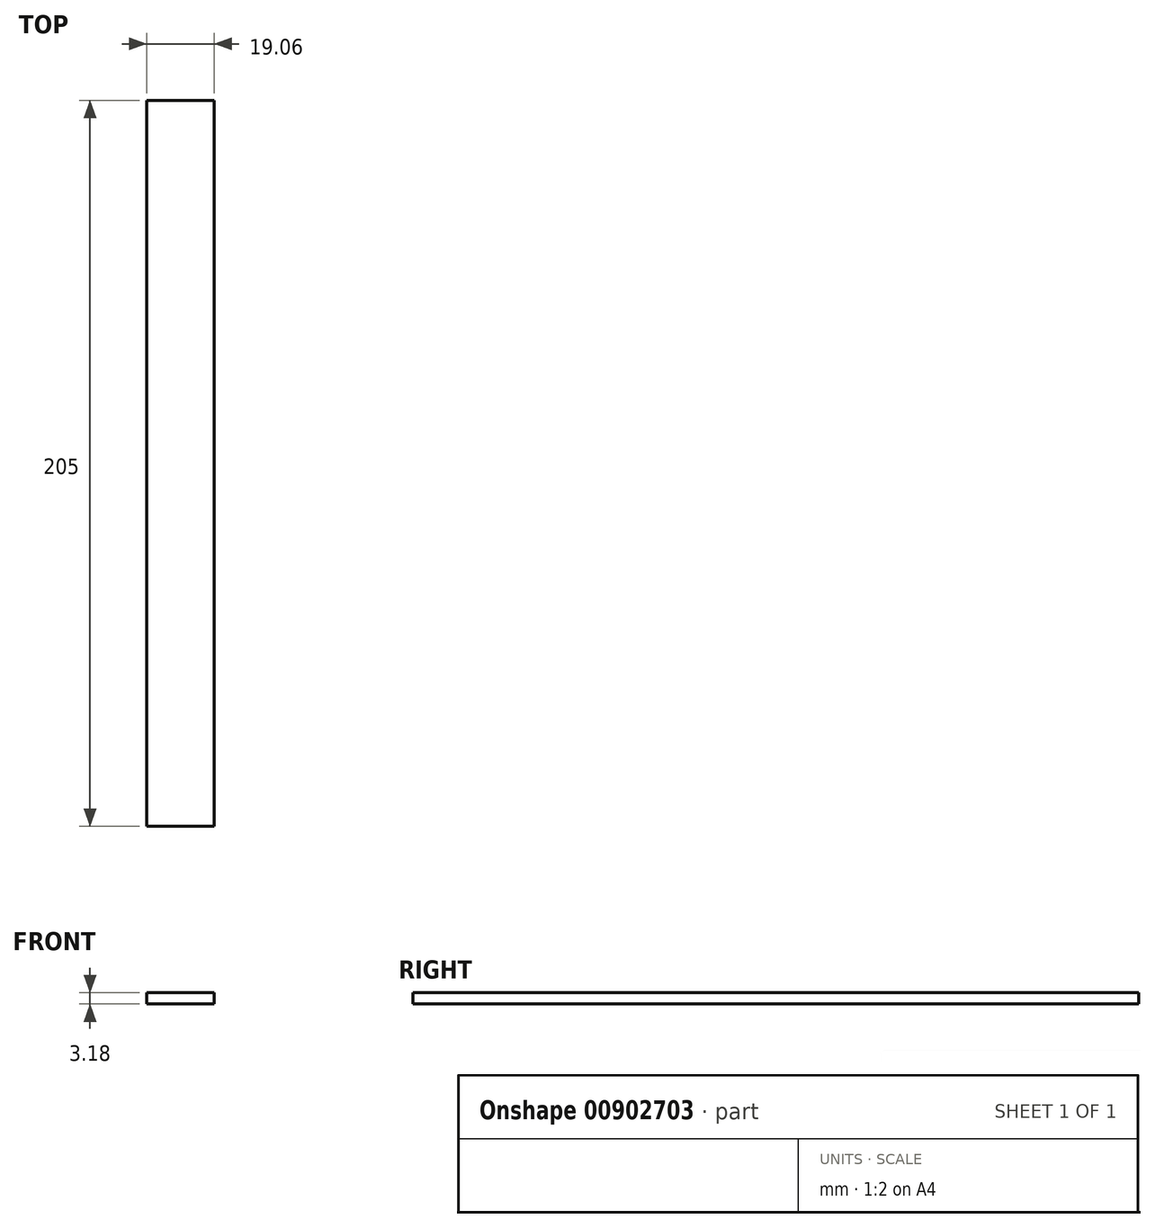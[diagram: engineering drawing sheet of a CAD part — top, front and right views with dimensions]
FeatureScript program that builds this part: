
annotation { "Feature Type Name" : "Feature", "Feature Type Description" : "" }
export const myFeature = defineFeature(function(context is Context, id is Id, definition is map)
    precondition{}
    {
        {
            var Q0;
            Q0=qCreatedBy(makeId("Front.planeOp"),FACE);
            var sketch = newSketch(context, id + "F0", { "sketchPlane" : qUnion([Q0])});
            skLineSegment(sketch, "E0.bottom", {"start": v(9.52, 1.59) * mm, "end": v(-9.53, 1.59) * mm});
            skLineSegment(sketch, "E0.top", {"start": v(9.52, -1.59) * mm, "end": v(-9.53, -1.59) * mm});
            skLineSegment(sketch, "E0.left", {"start": v(9.52, 1.59) * mm, "end": v(9.52, -1.59) * mm});
            skLineSegment(sketch, "E0.right", {"start": v(-9.53, 1.59) * mm, "end": v(-9.53, -1.59) * mm});
            skPoint(sketch, "E0.middle", {"position": v(0, 0) * mm});
            skSolve(sketch);
        }
        {
            var Q0;
            Q0=qSketchRegion(id+"F0",true);
            extrude(context, id + "F1", {"entities" : qUnion([Q0]), "depth" : 205 * mm, "offsetDistance" : 25 * mm});
        }
    });
